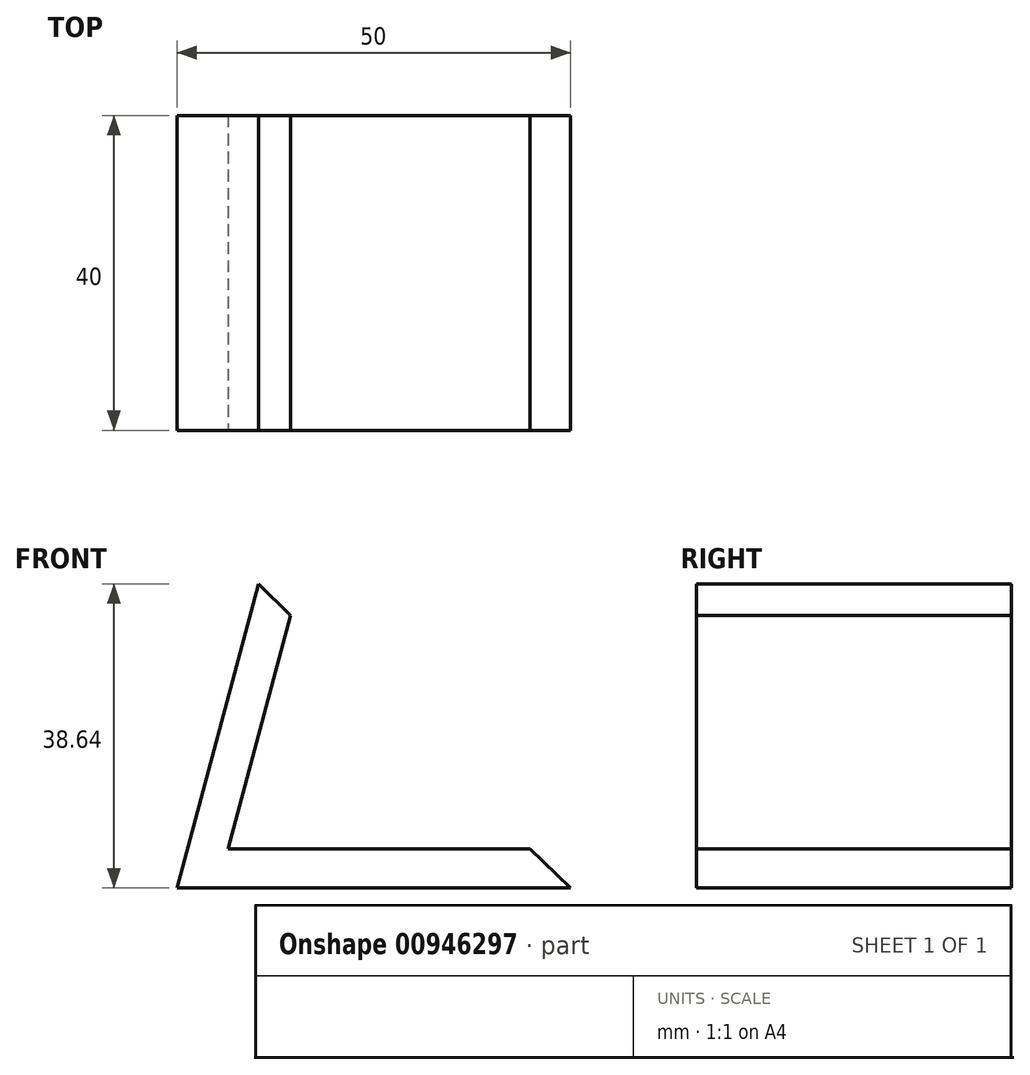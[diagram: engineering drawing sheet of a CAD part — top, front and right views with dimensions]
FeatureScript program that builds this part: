
annotation { "Feature Type Name" : "Feature", "Feature Type Description" : "" }
export const myFeature = defineFeature(function(context is Context, id is Id, definition is map)
    precondition{}
    {
        {
            var Q0;
            Q0=qCreatedBy(makeId("Front.planeOp"),FACE);
            var sketch = newSketch(context, id + "F0", { "sketchPlane" : qUnion([Q0])});
            skLineSegment(sketch, "E0", {"start": v(0, 0) * mm, "end": v(10.35, 38.64) * mm});
            skLineSegment(sketch, "E1", {"start": v(0, 0) * mm, "end": v(50, 0) * mm});
            skLineSegment(sketch, "E2", {"start": v(10.35, 38.64) * mm, "end": v(50, 0) * mm});
            skSolve(sketch);
        }
        {
            var Q0;
            Q0=makeQuery(id+"F0.imprint","IMPRINT",FACE,{"disambiguationData":[TD([[makeQuery(id+"F0.imprint","IMPRINT",EDGE,{"derivedFrom":sQuery(id+"F0.wireOp",EDGE,"E0")}),-1.0]])]});
            extrude(context, id + "F1", {"entities" : qUnion([Q0]), "depth" : 40 * mm, "offsetDistance" : 25 * mm});
        }
        {
            var Q0;
            Q0=makeQuery(id+"F1.opExtrude","CAP_FACE",FACE,{"disambiguationData":[OSD([sQuery(id+"F0.wireOp",EDGE,"E0"),sQuery(id+"F0.wireOp",EDGE,"E1"),sQuery(id+"F0.wireOp",EDGE,"E2")])],"isStart":false});
            var sketch = newSketch(context, id + "F2", { "sketchPlane" : qUnion([Q0])});
            skLineSegment(sketch, "E3.0", {"start": v(14.46, 34.64) * mm, "end": v(44.87, 5) * mm});
            skLineSegment(sketch, "E4.0", {"start": v(0, 0) * mm, "end": v(50, 0) * mm});
            skLineSegment(sketch, "E5.0", {"start": v(0, 0) * mm, "end": v(10.35, 38.64) * mm});
            skLineSegment(sketch, "E6.trimOffspring", {"start": v(6.52, 5) * mm, "end": v(44.87, 5) * mm});
            skLineSegment(sketch, "E7.trimOffspring", {"start": v(6.52, 5) * mm, "end": v(14.46, 34.64) * mm});
            skSolve(sketch);
        }
        {
            var Q0;
            Q0=makeQuery(id+"F2.imprint","IMPRINT",FACE,{"disambiguationData":[TD([[makeQuery(id+"F2.imprint","IMPRINT",EDGE,{"derivedFrom":sQuery(id+"F2.wireOp",EDGE,"E3.0")}),-1.0]])]});
            extrude(context, id + "F3", {"entities" : qUnion([Q0]), "operationType" : NewBodyOperationType.REMOVE, "oppositeDirection" : true, "depth" : 53 * mm, "offsetDistance" : 25 * mm});
        }
    });
